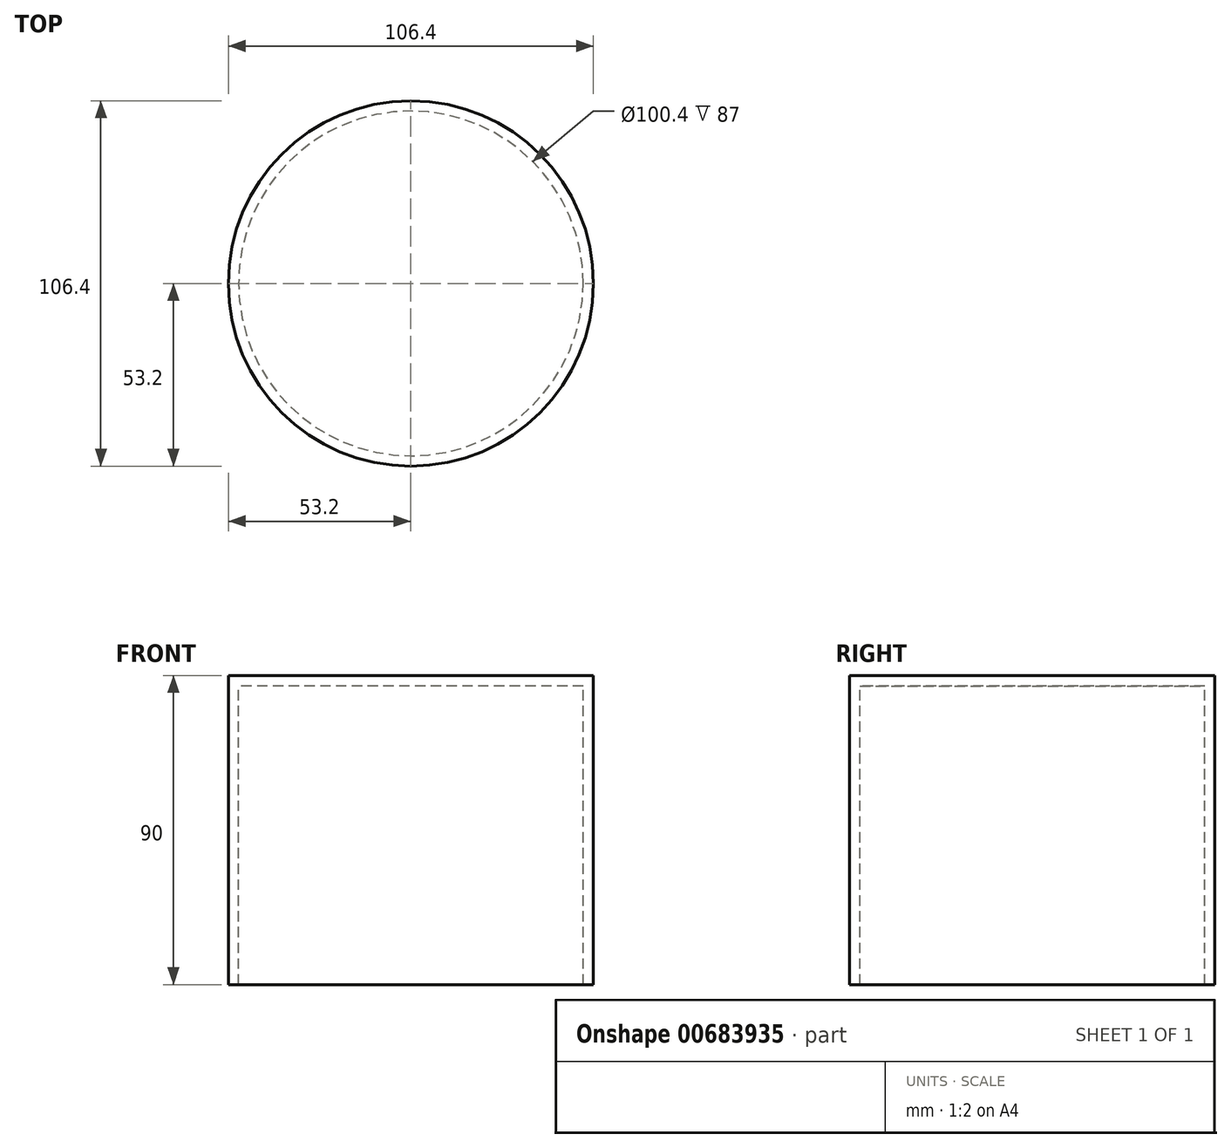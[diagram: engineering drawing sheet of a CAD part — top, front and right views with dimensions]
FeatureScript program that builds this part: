
annotation { "Feature Type Name" : "Feature", "Feature Type Description" : "" }
export const myFeature = defineFeature(function(context is Context, id is Id, definition is map)
    precondition{}
    {
        {
            var Q0;
            Q0=qCreatedBy(makeId("Top.planeOp"),FACE);
            var sketch = newSketch(context, id + "F0", { "sketchPlane" : qUnion([Q0])});
            skCircle(sketch, "E0", {"center": v(0, 0) * mm, "radius": 53.2 * mm});
            skCircle(sketch, "E1.0", {"center": v(0, 0) * mm, "radius": 50.2 * mm});
            skSolve(sketch);
        }
        {
            var Q0;
            Q0=makeQuery(id+"F0.imprint","IMPRINT",FACE,{"disambiguationData":[TD([[makeQuery(id+"F0.imprint","IMPRINT",EDGE,{"derivedFrom":sQuery(id+"F0.wireOp",EDGE,"E1.0")}),1.0]])]});
            extrude(context, id + "F1", {"entities" : qUnion([Q0]), "oppositeDirection" : true, "depth" : 3 * mm, "offsetDistance" : 25 * mm});
        }
        {
            var Q0;
            Q0 = qSketchRegion(id + "F0", true);
            extrude(context, id + "F2", {"entities" : qUnion([Q0]), "operationType" : NewBodyOperationType.ADD, "oppositeDirection" : true, "depth" : 90 * mm, "offsetDistance" : 25 * mm});
        }
    });
